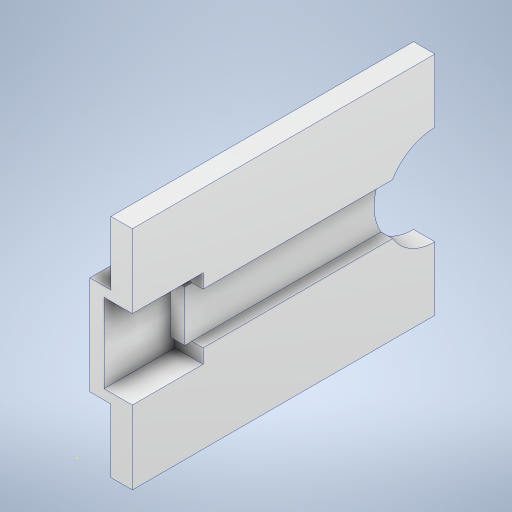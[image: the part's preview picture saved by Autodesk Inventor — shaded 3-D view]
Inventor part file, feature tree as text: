
AUTODESK INVENTOR PART (.ipt)
format: ipt  version: 2024 (Build 280153000, 153)  size: 348,672 bytes
history: native  units: mm
features: sketch x8, extrude x7
ambient origin geometry x8: Origin, YZ Plane, XZ Plane, XY Plane, X Axis, Y Axis, Z Axis, Center Point
bodies: Solid1 (feature_tree)
feature tree (15):
  extrude  "Extrusion1"  Depth=160.0mm TaperAngle=0.0deg
  extrude  "Extrusion2"  Depth=25.0mm
  extrude  "Extrusion4"  Depth=45.0mm
  extrude  "Extrusion5"  Depth=8.0mm
  sketch  "Sketch7"  dims[d10=36.0mm d11=80.0mm]
  extrude  "Extrusion6"  Depth=36.0mm
  extrude  "Extrusion7"  Depth=150.0mm TaperAngle=0.0deg
  extrude  "Extrusion8"  Depth=30.0mm
  sketch  "Sketch1"  dims[d0=550.0mm d1=160.0mm d2=0.0mm]
  sketch  "Sketch2"  dims[d4=25.0mm d5=25.0mm]
  sketch  "Sketch5"  dims[d6=0.0mm d7=45.0mm]
  sketch  "Sketch6"  dims[d8=45.0mm d9=8.0mm]
  sketch  "Sketch8"  dims[d12=80.0mm d13=150.0mm d14=0.0mm]
  sketch  "Sketch9"  dims[d15=30.0mm d28=39.130435mm]
  sketch  "Sketch10"  dims[d30=160.0mm d31=70.0mm d32=100.0mm d33=0.0mm d34=12.0mm d36=20.0mm d37=0.0mm d38=10.0mm d39=10.0mm d40=50.0mm d41=20.0mm d42=0.0mm d43=45.05mm d44=45.05mm d45=60.0mm d46=10.0mm d47=0.0mm d48=10.0mm d49=10.0mm d50=10.0mm d51=0.0mm]
